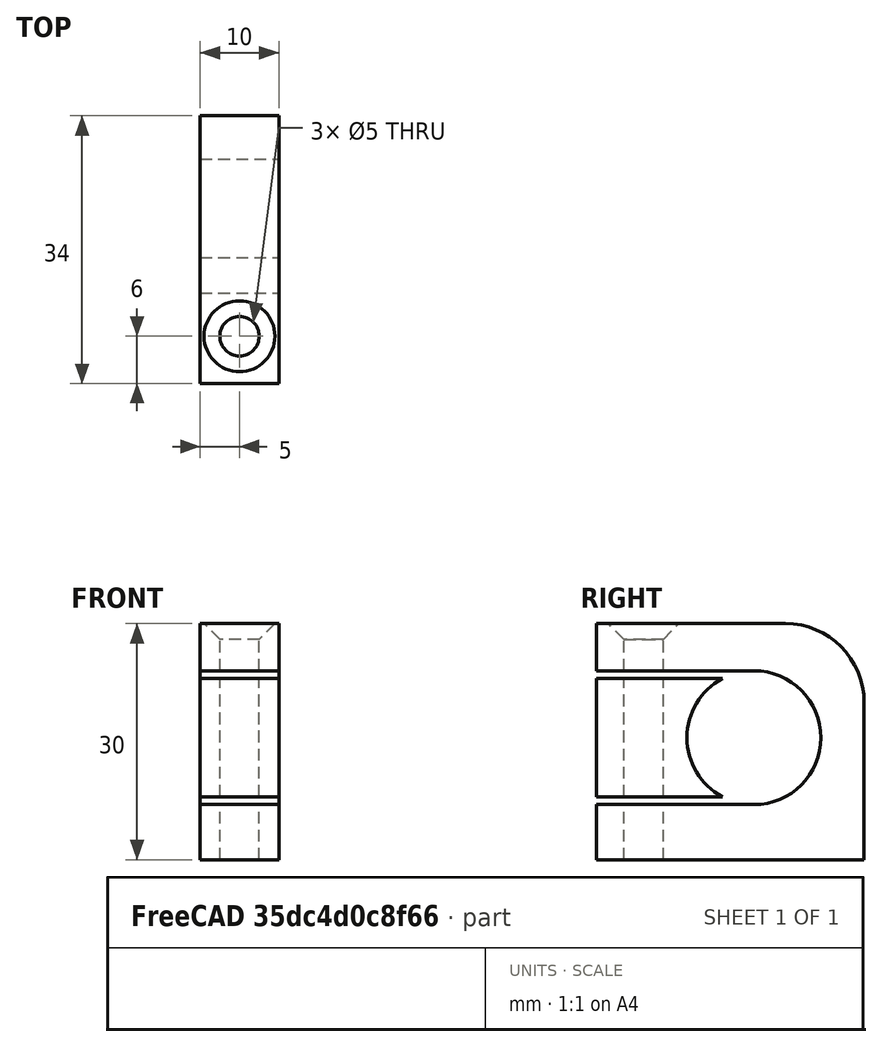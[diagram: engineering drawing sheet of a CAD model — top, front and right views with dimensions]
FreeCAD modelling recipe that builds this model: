
FCSTD DOCUMENT  (FreeCAD 0.17R13541 (Git))
Label: 16mm-cable-clamp
License: All rights reserved
LicenseURL: http://en.wikipedia.org/wiki/All_rights_reserved
objects: Part::Cylinder×4, Part::Box×3, Part::MultiFuse×2, Part::Cut×2, Part::Chamfer×1, Part::Fillet×1
note: 13 computed .brp shape members not serialized (recipe doc carries the construction recipe); baked Part::Feature solids carry a one-line shape summary decoded from their .brp

FEATURE [Part::Cylinder] Cylinder
  Angle = 360
  AttacherType = Attacher::AttachEngine3D
  Height = 37
  Placement = pos=(0,0,-1) rot=(0,0,1;0rad)
  Radius = 2.5
FEATURE [Part::Box] Box  label="Cube"
  AttacherType = Attacher::AttachEngine3D
  Height = 30
  Length = 10
  Placement = pos=(-5,-6,0) rot=(0,0,1;0rad)
  Width = 34
FEATURE [Part::Cylinder] Cylinder001
  Angle = 360
  AttacherType = Attacher::AttachEngine3D
  Height = 30
  Placement = pos=(-14,14,15.5) rot=(0,1,0;1.5708rad)
  Radius = 8.5
FEATURE [Part::Box] Box001  label="Cube001"
  AttacherType = Attacher::AttachEngine3D
  Height = 17
  Length = 15
  Placement = pos=(-7,-6,7) rot=(0,0,1;0rad)
  Width = 20
FEATURE [Part::Cylinder] Cylinder002
  Angle = 360
  AttacherType = Attacher::AttachEngine3D
  Height = 30
  Placement = pos=(-14,14,15.5) rot=(0,1,0;1.5708rad)
  Radius = 8.5
FEATURE [Part::Box] Box002  label="Cube002"
  AttacherType = Attacher::AttachEngine3D
  Height = 15
  Length = 10
  Placement = pos=(-5,-6,8) rot=(0,0,1;0rad)
  Width = 20
FEATURE [Part::Cylinder] Cylinder003
  Angle = 360
  AttacherType = Attacher::AttachEngine3D
  Height = 37
  Placement = pos=(0,0,-1) rot=(0,0,1;0rad)
  Radius = 2.5
FEATURE [Part::MultiFuse] Fusion
  Shapes = -> [Box001,Cylinder001,Cylinder]
FEATURE [Part::Cut] Cut
  Base = -> Box
  Tool = -> Fusion
FEATURE [Part::Chamfer] Chamfer
  Base = -> Cut
  Edges = 1 edges r=2: [Edge24]
FEATURE [Part::Fillet] Fillet
  Base = -> Chamfer
  Edges = 1 edges r=10: [Edge3]
FEATURE [Part::MultiFuse] Fusion001
  Shapes = -> [Cylinder002,Cylinder003]
FEATURE [Part::Cut] Cut001
  Base = -> Box002
  Tool = -> Fusion001
